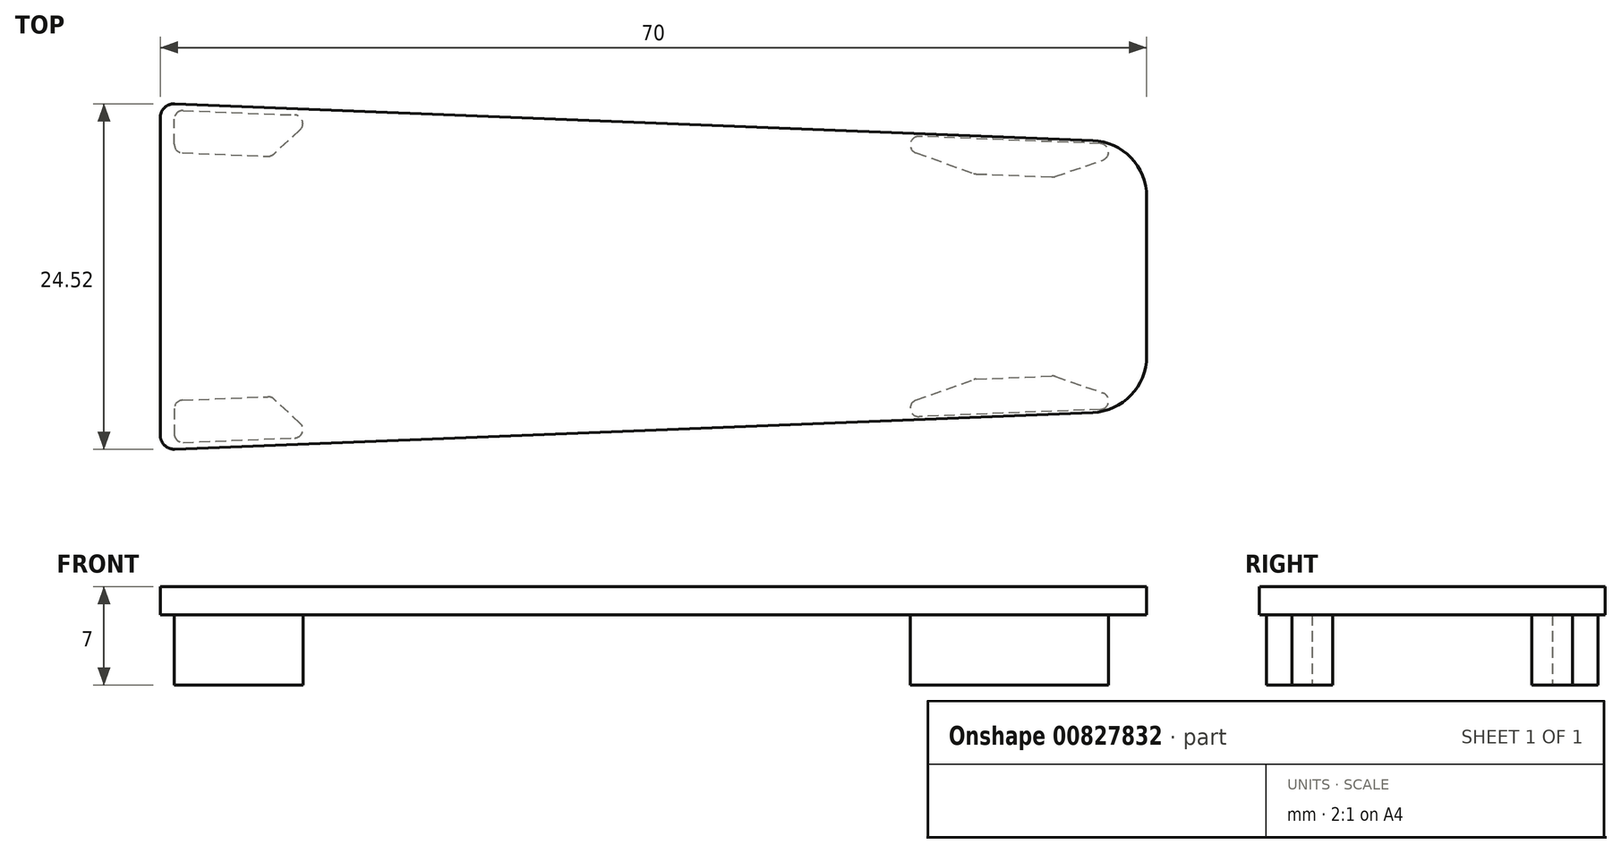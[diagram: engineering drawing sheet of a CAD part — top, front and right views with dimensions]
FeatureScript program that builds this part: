
annotation { "Feature Type Name" : "Feature", "Feature Type Description" : "" }
export const myFeature = defineFeature(function(context is Context, id is Id, definition is map)
    precondition{}
    {
        {
            var Q0;
            Q0=qCreatedBy(makeId("Top.planeOp"),FACE);
            var sketch = newSketch(context, id + "F0", { "sketchPlane" : qUnion([Q0])});
            skLineSegment(sketch, "E0", {"start": v(0, 0) * mm, "end": v(0, 12.3) * mm});
            skLineSegment(sketch, "E1", {"start": v(0, 12.3) * mm, "end": v(70, 9.5) * mm});
            skLineSegment(sketch, "E2", {"start": v(70, 9.5) * mm, "end": v(70, 0) * mm});
            skLineSegment(sketch, "E3", {"start": v(70, 0) * mm, "end": v(0, 0) * mm});
            skSolve(sketch);
        }
        {
            var Q0;
            Q0 = qSketchRegion(id + "F0", true);
            extrude(context, id + "F1", {"entities" : qUnion([Q0]), "depth" : 2 * mm, "offsetDistance" : 25 * mm});
        }
        {
            var Q0;
            Q0=makeQuery(id+"F1.opExtrude","CAP_FACE",FACE,{"disambiguationData":[OSD([sQuery(id+"F0.wireOp",EDGE,"E0"),sQuery(id+"F0.wireOp",EDGE,"E1"),sQuery(id+"F0.wireOp",EDGE,"E2"),sQuery(id+"F0.wireOp",EDGE,"E3")])],"isStart":false});
            var sketch = newSketch(context, id + "F2", { "sketchPlane" : qUnion([Q0])});
            skLineSegment(sketch, "E4", {"start": v(1, 8.8) * mm, "end": v(1, 11.8) * mm});
            skLineSegment(sketch, "E5", {"start": v(1, 11.8) * mm, "end": v(11, 11.4) * mm});
            skLineSegment(sketch, "E6", {"start": v(11, 11.4) * mm, "end": v(7.88, 8.52) * mm});
            skLineSegment(sketch, "E7", {"start": v(69.9, 9.3) * mm, "end": v(49.92, 10.1) * mm});
            skLineSegment(sketch, "E8", {"start": v(49.92, 10.1) * mm, "end": v(57.8, 7.28) * mm});
            skLineSegment(sketch, "E9", {"start": v(57.8, 7.28) * mm, "end": v(63.4, 7.06) * mm});
            skLineSegment(sketch, "E10", {"start": v(63.4, 7.06) * mm, "end": v(69.9, 9.3) * mm});
            skLineSegment(sketch, "E11", {"start": v(1, 8.8) * mm, "end": v(7.88, 8.52) * mm});
            skSolve(sketch);
        }
        {
            var Q0;
            Q0=makeQuery(id+"F2.imprint","IMPRINT",FACE,{"disambiguationData":[TD([[makeQuery(id+"F2.imprint","IMPRINT",EDGE,{"derivedFrom":sQuery(id+"F2.wireOp",EDGE,"E4")}),-1.0]])]});
            var Q1;
            Q1=makeQuery(id+"F2.imprint","IMPRINT",FACE,{"disambiguationData":[TD([[makeQuery(id+"F2.imprint","IMPRINT",EDGE,{"derivedFrom":sQuery(id+"F2.wireOp",EDGE,"E7")}),1.0]])]});
            extrude(context, id + "F3", {"entities" : qUnion([Q0, Q1]), "operationType" : NewBodyOperationType.ADD, "oppositeDirection" : true, "depth" : 7 * mm, "offsetDistance" : 25 * mm});
        }
        {
            var Q0;
            Q0=makeQuery(id+"F3.opExtrude","SWEPT_EDGE",EDGE,{"disambiguationData":[OSD([sQuery(id+"F2.wireOp",EDGE,"E4"),sQuery(id+"F2.wireOp",EDGE,"E5")])]});
            var Q1;
            Q1=makeQuery(id+"F3.opExtrude","SWEPT_EDGE",EDGE,{"disambiguationData":[OSD([sQuery(id+"F2.wireOp",EDGE,"E5"),sQuery(id+"F2.wireOp",EDGE,"E6")])]});
            var Q2;
            Q2=makeQuery(id+"F3.opExtrude","SWEPT_EDGE",EDGE,{"disambiguationData":[OSD([sQuery(id+"F2.wireOp",EDGE,"E4"),sQuery(id+"F2.wireOp",EDGE,"E6")])]});
            var Q3;
            Q3=makeQuery(id+"F3.opExtrude","SWEPT_EDGE",EDGE,{"disambiguationData":[OSD([sQuery(id+"F2.wireOp",EDGE,"E7"),sQuery(id+"F2.wireOp",EDGE,"E10")])]});
            var Q4;
            Q4=makeQuery(id+"F3.opExtrude","SWEPT_EDGE",EDGE,{"disambiguationData":[OSD([sQuery(id+"F2.wireOp",EDGE,"E7"),sQuery(id+"F2.wireOp",EDGE,"E8")])]});
            var Q5;
            Q5=makeQuery(id+"F3.opExtrude","SWEPT_EDGE",EDGE,{"disambiguationData":[OSD([sQuery(id+"F2.wireOp",EDGE,"E9"),sQuery(id+"F2.wireOp",EDGE,"E10")])]});
            var Q6;
            Q6=makeQuery(id+"F3.opExtrude","SWEPT_EDGE",EDGE,{"disambiguationData":[OSD([sQuery(id+"F2.wireOp",EDGE,"E8"),sQuery(id+"F2.wireOp",EDGE,"E9")])]});
            fillet(context, id + "F4", {"entities" : qUnion([Q0, Q1, Q2, Q3, Q4, Q5, Q6]), "radius" : .6 * mm, "tangentPropagation" : true, "allowEdgeOverflow" : false});
        }
        {
            var Q0;
            Q0=makeQuery(id+"F1.opExtrude","SWEPT_EDGE",EDGE,{"disambiguationData":[OSD([sQuery(id+"F0.wireOp",EDGE,"E1"),sQuery(id+"F0.wireOp",EDGE,"E2")])]});
            fillet(context, id + "F5", {"entities" : qUnion([Q0]), "radius" : 4 * mm, "tangentPropagation" : true, "allowEdgeOverflow" : false});
        }
        {
            var Q0;
            Q0=makeQuery(id+"F1.opExtrude","SWEPT_EDGE",EDGE,{"disambiguationData":[OSD([sQuery(id+"F0.wireOp",EDGE,"E0"),sQuery(id+"F0.wireOp",EDGE,"E1")])]});
            fillet(context, id + "F6", {"entities" : qUnion([Q0]), "radius" : 1 * mm, "tangentPropagation" : true, "allowEdgeOverflow" : false});
        }
        {
            var Q0;
            Q0=makeQuery(id+"F1.opExtrude","SWEPT_BODY",BODY,{"disambiguationData":[OSD([sQuery(id+"F0.wireOp",EDGE,"E0"),sQuery(id+"F0.wireOp",EDGE,"E1"),sQuery(id+"F0.wireOp",EDGE,"E2"),sQuery(id+"F0.wireOp",EDGE,"E3")])]});
            var Q1;
            Q1=qCreatedBy(makeId("Front.planeOp"),FACE);
            mirror(context, id + "F7", {"operationType" : NewBodyOperationType.ADD, "entities" : qUnion([Q0]), "mirrorPlane" : qUnion([Q1])});
        }
    });
